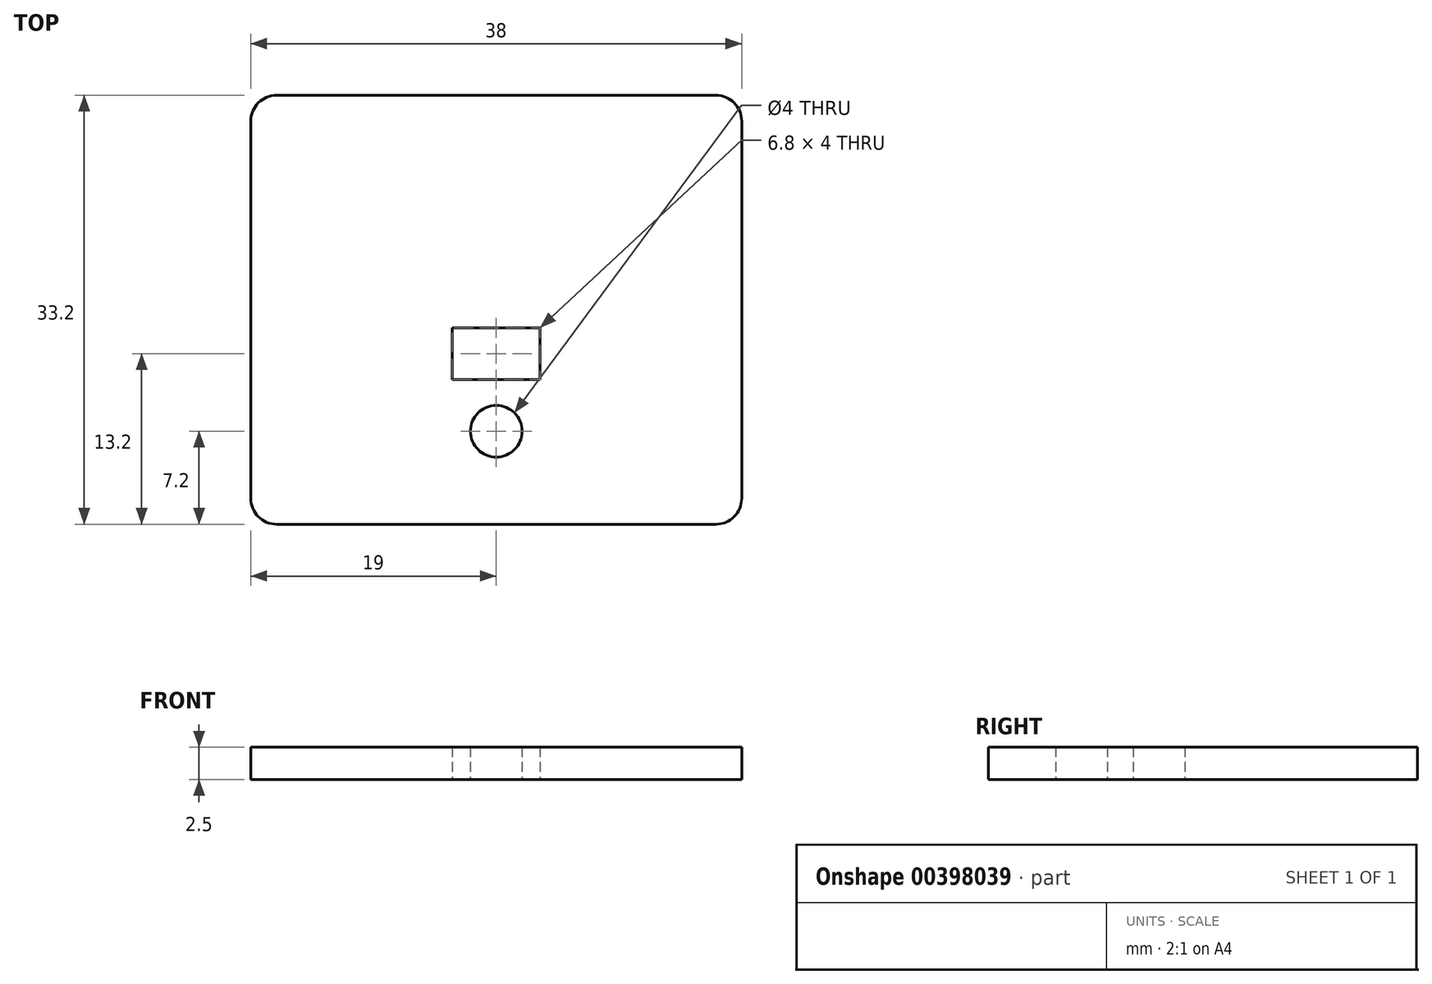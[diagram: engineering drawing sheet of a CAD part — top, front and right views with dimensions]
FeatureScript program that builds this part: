
annotation { "Feature Type Name" : "Feature", "Feature Type Description" : "" }
export const myFeature = defineFeature(function(context is Context, id is Id, definition is map)
    precondition{}
    {
        {
            var Q0;
            Q0=qCreatedBy(makeId("Top.planeOp"),FACE);
            var sketch = newSketch(context, id + "F0", { "sketchPlane" : qUnion([Q0])});
            skLineSegment(sketch, "E0.bottom", {"start": v(-17, 16.6) * mm, "end": v(17, 16.6) * mm});
            skLineSegment(sketch, "E0.top", {"start": v(-17, -16.6) * mm, "end": v(17, -16.6) * mm});
            skLineSegment(sketch, "E0.left", {"start": v(-19, 14.6) * mm, "end": v(-19, -14.6) * mm});
            skLineSegment(sketch, "E0.right", {"start": v(19, 14.6) * mm, "end": v(19, -14.6) * mm});
            skPoint(sketch, "E1.visualSharp", {"position": v(-19, 16.6) * mm});
            skArc(sketch, "E1.filletArc", {"start": v(-17, 16.6) * mm, "mid": v(-18.41, 16.01) * mm, "end": v(-19, 14.6) * mm});
            skPoint(sketch, "E2.visualSharp", {"position": v(19, 16.6) * mm});
            skArc(sketch, "E2.filletArc", {"start": v(19, 14.6) * mm, "mid": v(18.41, 16.01) * mm, "end": v(17, 16.6) * mm});
            skPoint(sketch, "E3.visualSharp", {"position": v(19, -16.6) * mm});
            skArc(sketch, "E3.filletArc", {"start": v(17, -16.6) * mm, "mid": v(18.41, -16.01) * mm, "end": v(19, -14.6) * mm});
            skPoint(sketch, "E4.visualSharp", {"position": v(-19, -16.6) * mm});
            skArc(sketch, "E4.filletArc", {"start": v(-19, -14.6) * mm, "mid": v(-18.41, -16.01) * mm, "end": v(-17, -16.6) * mm});
            skCircle(sketch, "E5", {"center": v(0, -9.4) * mm, "radius": 2 * mm});
            skLineSegment(sketch, "E6.bottom", {"start": v(-3.4, -1.4) * mm, "end": v(3.4, -1.4) * mm});
            skLineSegment(sketch, "E6.top", {"start": v(-3.4, -5.4) * mm, "end": v(3.4, -5.4) * mm});
            skLineSegment(sketch, "E6.left", {"start": v(-3.4, -1.4) * mm, "end": v(-3.4, -5.4) * mm});
            skLineSegment(sketch, "E6.right", {"start": v(3.4, -1.4) * mm, "end": v(3.4, -5.4) * mm});
            skSolve(sketch);
        }
        {
            var Q0;
            Q0=makeQuery(id+"F0.imprint","IMPRINT",FACE,{"disambiguationData":[TD([[makeQuery(id+"F0.imprint","IMPRINT",EDGE,{"derivedFrom":sQuery(id+"F0.wireOp",EDGE,"E0.bottom")}),-1.0]])]});
            extrude(context, id + "F1", {"entities" : qUnion([Q0]), "depth" : 2.5 * mm});
        }
    });
